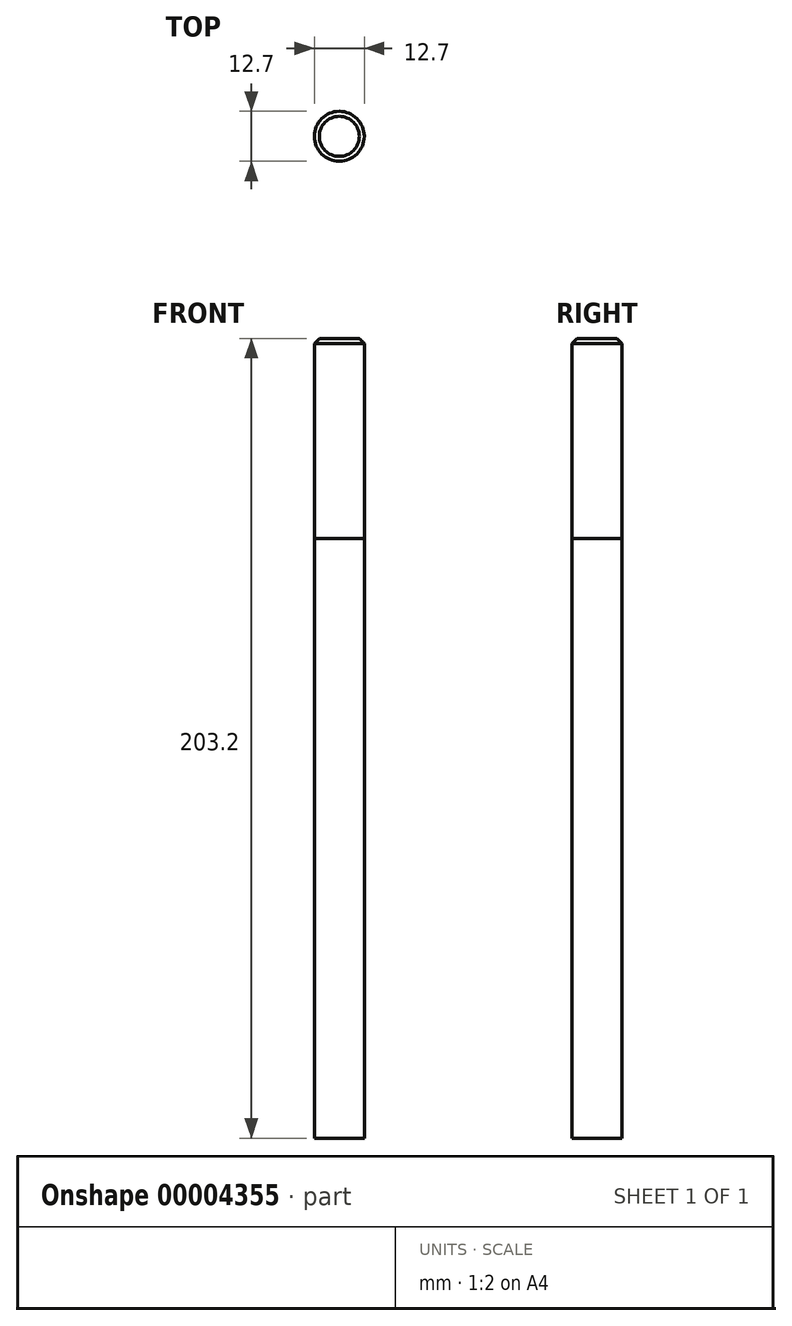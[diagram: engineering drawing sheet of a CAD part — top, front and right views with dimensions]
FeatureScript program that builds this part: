
annotation { "Feature Type Name" : "Feature", "Feature Type Description" : "" }
export const myFeature = defineFeature(function(context is Context, id is Id, definition is map)
    precondition{}
    {
        {
            var Q0;
            Q0=qCreatedBy(makeId("Top.planeOp"),FACE);
            var sketch = newSketch(context, id + "F0", { "sketchPlane" : qUnion([Q0])});
            skCircle(sketch, "E0", {"center": v(0, 0) * mm, "radius": 6.35 * mm});
            skSolve(sketch);
        }
        {
            var Q0;
            Q0=makeQuery(id+"F0.imprint","IMPRINT",FACE,{"disambiguationData":[TD([[makeQuery(id+"F0.imprint","IMPRINT",EDGE,{"derivedFrom":sQuery(id+"F0.wireOp",EDGE,"E0")}),1.0]])]});
            extrude(context, id + "F1", {"entities" : qUnion([Q0]), "depth" : 203.2 * mm});
        }
        {
            var Q0;
            Q0=makeQuery(id+"F1.opExtrude","CAP_EDGE",EDGE,{"disambiguationData":[OSD([sQuery(id+"F0.wireOp",EDGE,"E0")])],"isStart":false});
            chamfer(context, id + "F2", {"entities" : qUnion([Q0]), "width" : 1.27 * mm, "tangentPropagation" : true});
        }
        {
            var Q0;
            Q0 = qSketchRegion(id + "F0", true);
            extrude(context, id + "F3", {"entities" : qUnion([Q0]), "depth" : 152.4 * mm});
        }
    });
